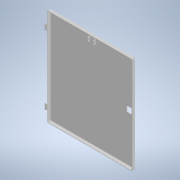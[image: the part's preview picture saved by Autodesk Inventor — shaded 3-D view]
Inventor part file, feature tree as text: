
AUTODESK INVENTOR PART (.ipt)
format: ipt  version: 2021 (Build 250183000, 183)  size: 230,912 bytes
history: native  units: mm
features: other x14, extrude x10, sketch x10
ambient origin geometry x8: Origin, YZ Plane, XZ Plane, XY Plane, X Axis, Y Axis, Z Axis, Center Point
bodies: Solid1 (feature_tree)
feature tree (34):
  extrude  "Extrusion1"  Depth=400.0mm TaperAngle=0.0deg
  extrude  "Extrusion2"  Depth=350.0mm TaperAngle=0.0deg
  extrude  "Extrusion3"  Depth=17.25mm TaperAngle=0.0deg
  extrude  "Extrusion4"  Depth=30.0mm TaperAngle=0.0deg
  extrude  "Extrusion5"  Depth=21.75mm TaperAngle=0.0deg
  extrude  "Extrusion6"  [1 undecoded]
  extrude  "Extrusion7"  [1 undecoded]
  extrude  "Extrusion8"  [1 undecoded]
  extrude  "Extrusion9"  [1 undecoded]
  extrude  "Extrusion10"  [1 undecoded]
  other  "door_to_hinge_XY"
  other  "door_to_hinge_YZ"
  other  "door_to_hinge_ZX"
  other  "door_to_hinge_X"
  other  "door_to_hinge_Y"
  other  "door_to_hinge_Z"
  other  "door_to_hinge_Center"
  other  "lock_XY"
  other  "lock_YZ"
  other  "lock_ZX"
  other  "lock_X"
  other  "lock_Y"
  other  "lock_Z"
  other  "lock_Center"
  sketch  "Sketch_2"  dims[d0=15.0mm d1=0.0mm d2=400.0mm d3=0.0mm]
  sketch  "Sketch_3"  dims[d4=350.0mm d5=0.0mm d6=15.5mm d7=0.0mm]
  sketch  "Sketch_4"  dims[d8=3.0mm d9=0.0mm d10=17.25mm d11=0.0mm]
  sketch  "Sketch_8"
  sketch  "Sketch_6"  dims[d12=30.0mm d13=0.0mm d14=30.0mm d15=0.0mm]
  sketch  "Sketch_9"
  sketch  "Sketch_10"
  sketch  "Sketch_11"
  sketch  "Sketch_12"
  sketch  "Sketch_7"  dims[d16=21.75mm d17=0.0mm d18=21.75mm d19=0.0mm]
note: 5 required parameter values undecoded (feature->parameter linkage not recoverable at this tier; creation-order binding heuristic only, values carry confidence <= 0.55)
